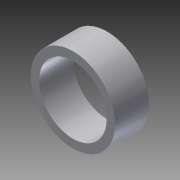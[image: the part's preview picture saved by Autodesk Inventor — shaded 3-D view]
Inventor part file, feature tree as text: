
AUTODESK INVENTOR PART (.ipt)
format: ipt  version: 2014 SP1 (Build 180222100, 222)  size: 83,456 bytes
history: native  units: in
note: dims shown in document units (in); Inventor stores cm internally (conversion verified against a paired STEP export)
features: extrude x1, sketch x1
ambient origin geometry x8: Origin, YZ Plane, XZ Plane, XY Plane, X Axis, Y Axis, Z Axis, Center Point
bodies: Solid1 (feature_tree)
feature tree (2):
  extrude  "Extrusion1"  Depth=0.253in
  sketch  "Sketch1"  dims[d0=0.5in d1=0.625in d2=0.253in d3=0.0in]
